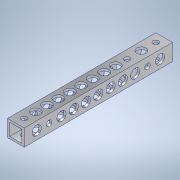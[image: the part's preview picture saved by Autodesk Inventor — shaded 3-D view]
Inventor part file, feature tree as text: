
AUTODESK INVENTOR PART (.ipt)
format: ipt  version: 2020.3 (Build 243373000, 373)  size: 231,424 bytes
history: native  units: mm
features: sketch x6, hole x5, other x1, extrude x1
ambient origin geometry x8: Origin, YZ Plane, XZ Plane, XY Plane, X Axis, Y Axis, Z Axis, Center Point
bodies: Body1 (feature_tree)
feature tree (13):
  other  "ソリッド1"
  extrude  "押し出し1"  Depth=9.0mm
  hole  "穴2"  [1 undecoded]
  hole  "穴3"  [1 undecoded]
  hole  "穴4"  [1 undecoded]
  hole  "穴5"  [1 undecoded]
  hole  "穴6"  [1 undecoded]
  sketch  "スケッチ1"
  sketch  "スケッチ3"
  sketch  "スケッチ4"
  sketch  "スケッチ5"
  sketch  "スケッチ6"
  sketch  "スケッチ7"
note: 5 required parameter values undecoded (feature->parameter linkage not recoverable at this tier; creation-order binding heuristic only, values carry confidence <= 0.55)
